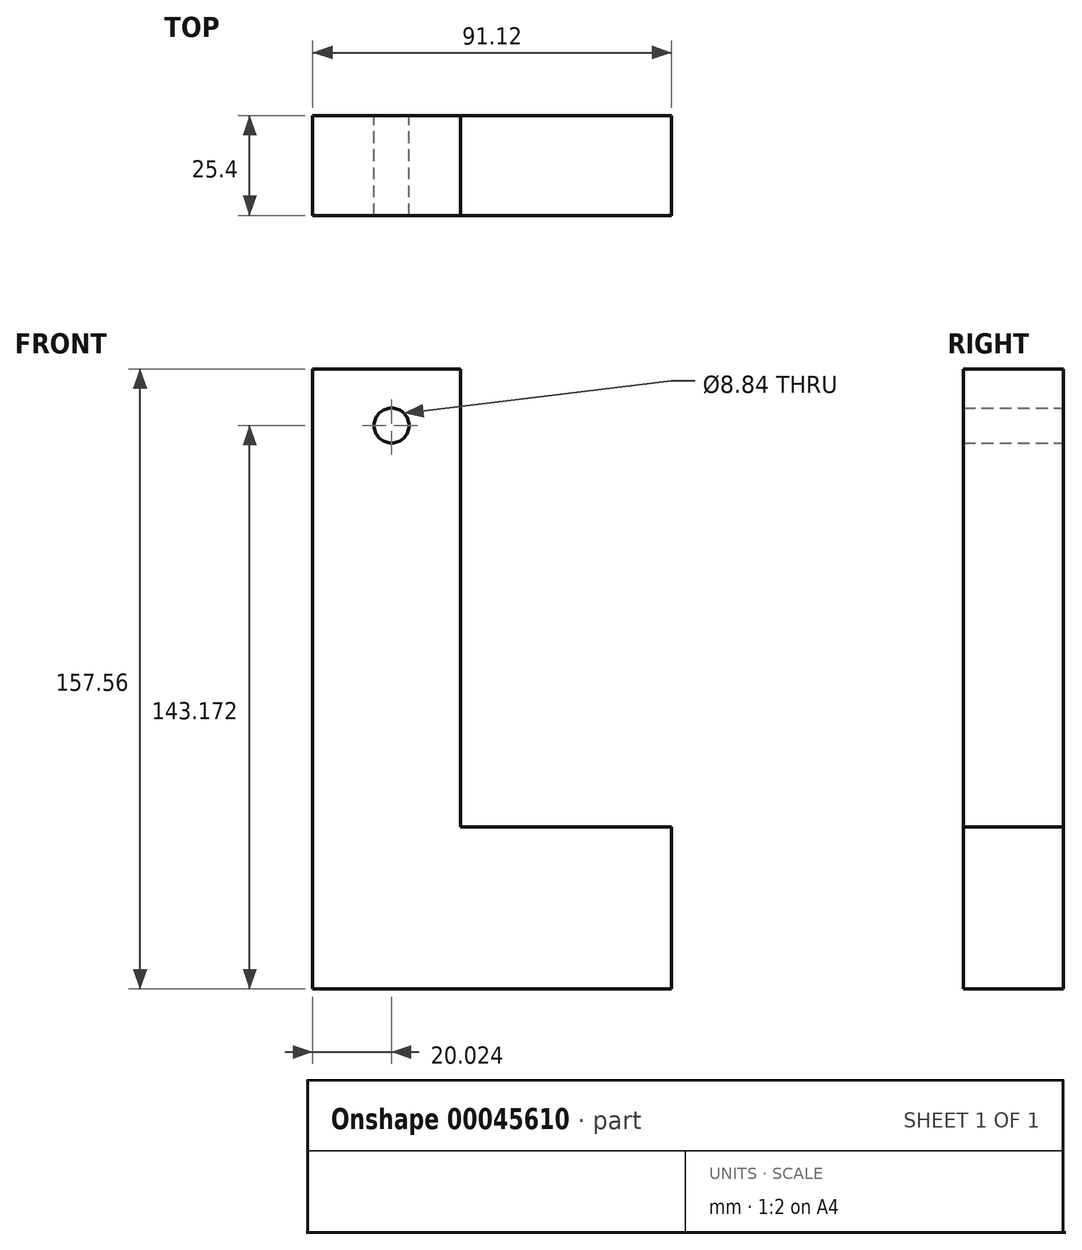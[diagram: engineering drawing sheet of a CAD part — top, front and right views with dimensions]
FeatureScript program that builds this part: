
annotation { "Feature Type Name" : "Feature", "Feature Type Description" : "" }
export const myFeature = defineFeature(function(context is Context, id is Id, definition is map)
    precondition{}
    {
        {
            var Q0;
            Q0=qCreatedBy(makeId("Front.planeOp"),FACE);
            var sketch = newSketch(context, id + "F1", { "sketchPlane" : qUnion([Q0])});
            skLineSegment(sketch, "E0.bottom", {"start": v(47.13, -29.9) * mm, "end": v(-44, -29.9) * mm});
            skLineSegment(sketch, "E0.top", {"start": v(47.13, 11.31) * mm, "end": v(-44, 11.31) * mm});
            skLineSegment(sketch, "E0.left", {"start": v(47.13, -29.9) * mm, "end": v(47.13, 11.31) * mm});
            skLineSegment(sketch, "E0.right", {"start": v(-44, -29.9) * mm, "end": v(-44, 11.31) * mm});
            skLineSegment(sketch, "E1.bottom", {"start": v(-44, 11.31) * mm, "end": v(-6.46, 11.31) * mm});
            skLineSegment(sketch, "E1.top", {"start": v(-44, 127.66) * mm, "end": v(-6.46, 127.66) * mm});
            skLineSegment(sketch, "E1.left", {"start": v(-44, 11.31) * mm, "end": v(-44, 127.66) * mm});
            skLineSegment(sketch, "E1.right", {"start": v(-6.46, 11.31) * mm, "end": v(-6.46, 127.66) * mm});
            skCircle(sketch, "E2", {"center": v(-23.97, 113.27) * mm, "radius": 4.42 * mm});
            skSolve(sketch);
        }
        {
            var Q0;
            Q0 = qSketchRegion(id + "F1", true);
            var Q1;
            Q1=makeQuery(id+"F1.imprint","IMPRINT",FACE,{"disambiguationData":[TD([[makeQuery(id+"F1.imprint","IMPRINT",EDGE,{"derivedFrom":sQuery(id+"F1.wireOp",EDGE,"E1.bottom")}),1.0]])]});
            var Q2;
            Q2=makeQuery(id+"F1.imprint","IMPRINT",FACE,{"disambiguationData":[TD([[makeQuery(id+"F1.imprint","IMPRINT",EDGE,{"derivedFrom":sQuery(id+"F1.wireOp",EDGE,"E0.bottom")}),-1.0]])]});
            extrude(context, id + "F0", {"entities" : qUnion([Q0, Q1, Q2]), "depth" : 25.4 * mm});
        }
    });
